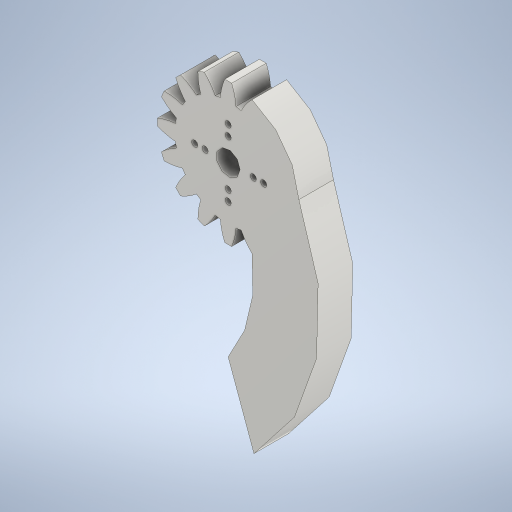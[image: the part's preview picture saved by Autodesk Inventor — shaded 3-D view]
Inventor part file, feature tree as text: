
AUTODESK INVENTOR PART (.ipt)
format: ipt  version: 2024 (Build 280153000, 153)  size: 674,816 bytes
history: native  units: mm (DEFAULTED — no unit token found)
features: other x7, extrude x3, plane x3, sketch x3, reference x1, projected_geometry x1
ambient origin geometry x8: Origin, YZ Plane, XZ Plane, XY Plane, X Axis, Y Axis, Z Axis, Center Point
bodies: Solid1 (feature_tree)
feature tree (18):
  extrude  "Extrusion1"  Depth=6.666667mm TaperAngle=0.0deg
  plane  "Work Plane2"
  plane  "Work Plane8"
  plane  "Work Plane9"
  other  "Spur Gear"
  extrude  "Extrusion2"  Depth=10.0mm TaperAngle=0.0deg
  extrude  "Extrusion3"  TaperAngle=0.0deg  [1 undecoded]
  sketch  "Sketch1"  dims[d0=27.3mm d1=6.666667mm d2=0.0mm]
  other  "Srf1"
  sketch  "Sketch3"  dims[d3=24.0mm d4=10.0mm d5=0.0mm]
  reference  "Reference1"
  sketch  "Sketch4"  dims[d16=23.4mm d17=0.0mm d34=1.963495mm d39=0.0mm d41=0.0mm d43=23.4mm d46=23.4mm d47=0.0mm d48=0.0mm d49=10.0mm d50=0.0mm d51=50.0mm d52=79.653867mm d53=54.037661mm d54=6.666667mm d55=0.0mm d61=3.490659mm d62=18.74711mm d63=13.672504mm d64=16.87961mm d65=22.118418mm]
  projected_geometry  "Projected Loop1"
  other  "Pitch Diameter"
  other  "<userpath> windows\Documents\Inventor\Robotska_roka\roka_asemb.iam"
  other  "roka_asemb.iam"
  other  "SG90 - Micro Servo 9g - Tower Pro:2"
  other  "SG90 - Micro Servo 9g - Tower Pro.4"
note: 1 required parameter value undecoded (feature->parameter linkage not recoverable at this tier; creation-order binding heuristic only, values carry confidence <= 0.55)
